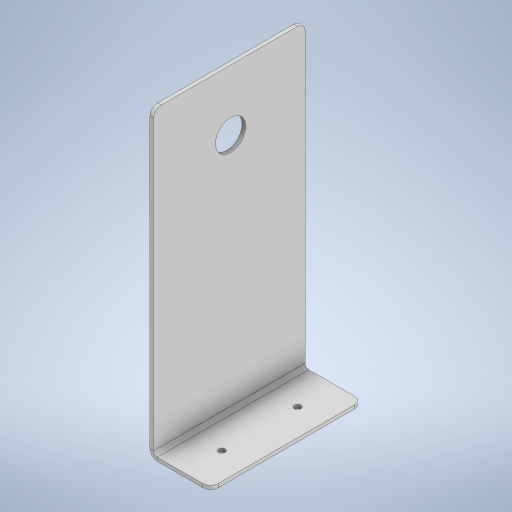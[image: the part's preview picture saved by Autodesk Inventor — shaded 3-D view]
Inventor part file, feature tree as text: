
AUTODESK INVENTOR PART (.ipt)
format: ipt  version: 2023 (Build 270158000, 158)  size: 271,872 bytes
history: native  units: in
note: dims shown in document units (in); Inventor stores cm internally (conversion verified against a paired STEP export)
features: sheet_metal_op x4, sketch x4, hole x2, other x2, chamfer x1
ambient origin geometry x8: Origin, YZ Plane, XZ Plane, XY Plane, X Axis, Y Axis, Z Axis, Center Point
bodies: Solid1 (feature_tree)
feature tree (13):
  sheet_metal_op  "Face1"
  sheet_metal_op  "Flange1"
  hole  "Hole1"  [1 undecoded]
  chamfer  "Corner Round1"
  hole  "Hole2"  [1 undecoded]
  sketch  "Sketch1"  dims[d0=2.0in d1=5.0in]
  other  "Plate1"
  sketch  "Sketch2"  dims[d2=0.12in d3=0.12in]
  other  "Plate2"
  sheet_metal_op  "Bend1"
  sheet_metal_op  "Corner1"
  sketch  "Sketch3"  dims[d4=0.06in]
  sketch  "Sketch4"  dims[d5=0.24in d6=0.12in d7=10.0in d8=90.0deg d9=0.12in d10=0.48in d11=0.12in d12=0.12in d13=0.217in d14=0.75in d15=0.2559in d16=0.1024in d17=0.5635in d18=0.12in d19=0.8108in d20=2.5in d21=1.25in d22=0.25in d23=2.54in d24=1.0in d25=0.75in d26=0.591in d27=0.169in d28=0.5635in d29=1.0in d30=0.8108in d31=2.0in]
note: 2 required parameter values undecoded (feature->parameter linkage not recoverable at this tier; creation-order binding heuristic only, values carry confidence <= 0.55)
